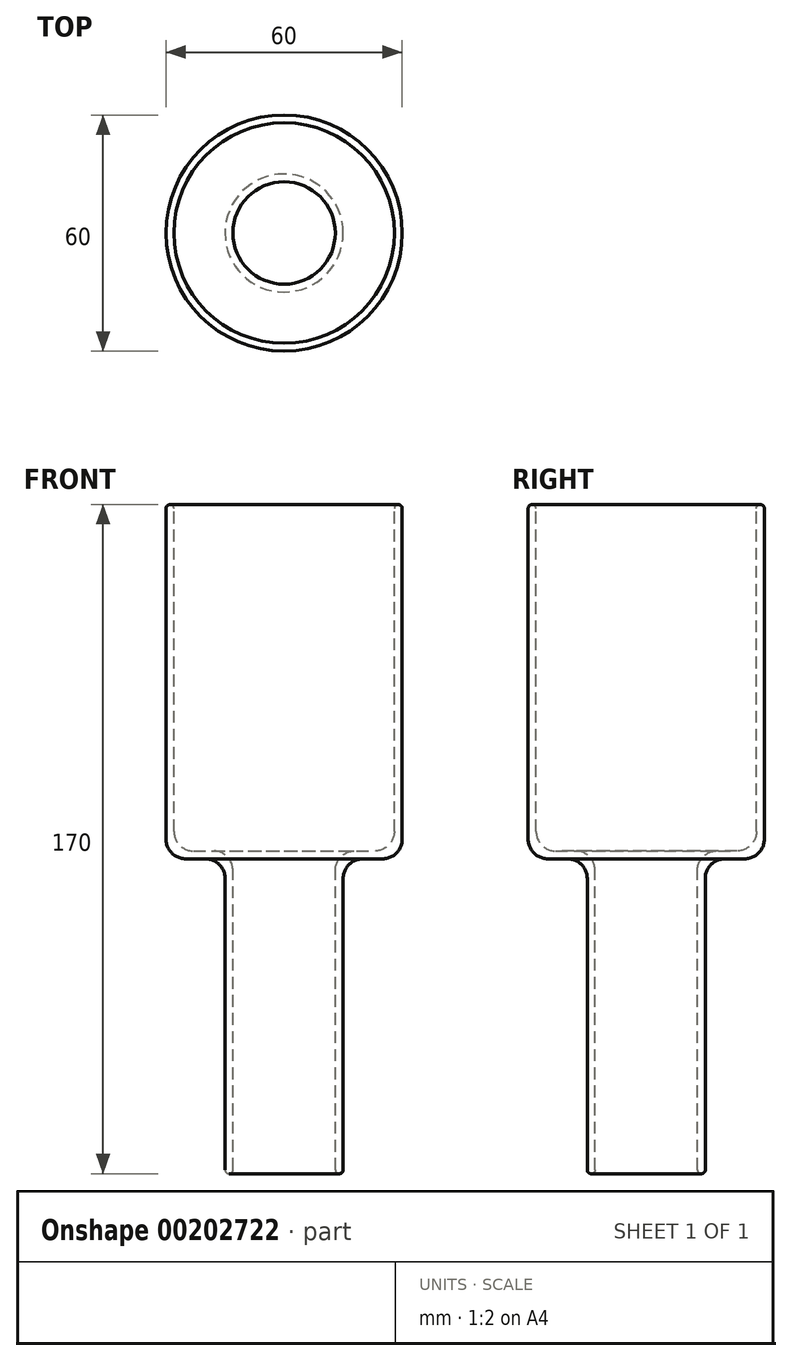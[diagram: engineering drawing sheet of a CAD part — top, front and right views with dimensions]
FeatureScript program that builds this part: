
annotation { "Feature Type Name" : "Feature", "Feature Type Description" : "" }
export const myFeature = defineFeature(function(context is Context, id is Id, definition is map)
    precondition{}
    {
        {
            var Q0;
            Q0=qCreatedBy(makeId("Front.planeOp"),FACE);
            var sketch = newSketch(context, id + "F0", { "sketchPlane" : qUnion([Q0])});
            skLineSegment(sketch, "E0", {"start": v(-28, 98.38) * mm, "end": v(-30, 98.38) * mm});
            skLineSegment(sketch, "E1", {"start": v(-30, 98.38) * mm, "end": v(-30, 8.38) * mm});
            skLineSegment(sketch, "E2", {"start": v(-30, 8.38) * mm, "end": v(-15, 8.38) * mm});
            skLineSegment(sketch, "E3", {"start": v(-15, 8.38) * mm, "end": v(-15, -71.62) * mm});
            skLineSegment(sketch, "E4", {"start": v(-15, -71.62) * mm, "end": v(-13, -71.62) * mm});
            skLineSegment(sketch, "E5.0", {"start": v(-13, 10.38) * mm, "end": v(-13, -71.62) * mm});
            skLineSegment(sketch, "E5.1", {"start": v(-28, 10.38) * mm, "end": v(-13, 10.38) * mm});
            skLineSegment(sketch, "E5.2", {"start": v(-28, 98.38) * mm, "end": v(-28, 10.38) * mm});
            skPoint(sketch, "E6.start.orphan", {"position": v(0, 98.38) * mm});
            skPoint(sketch, "E7.orphan", {"position": v(0, -71.62) * mm});
            skLineSegment(sketch, "E8", {"start": v(0, 98.38) * mm, "end": v(0, -71.62) * mm});
            skSolve(sketch);
        }
        {
            var Q0;
            Q0 = qSketchRegion(id + "F0", true);
            var Q1;
            Q1=sQuery(id+"F0.wireOp",EDGE,"E8");
            revolve(context, id + "F1", {"entities" : qUnion([Q0]), "axis" : qUnion([Q1]), "revolveType" : RevolveType.FULL});
        }
        {
            var Q0;
            Q0=makeQuery(id+"F1.opRevolve","SWEPT_EDGE",EDGE,{"disambiguationData":[OSD([sQuery(id+"F0.wireOp",EDGE,"E1"),sQuery(id+"F0.wireOp",EDGE,"E2")])]});
            var Q1;
            Q1=makeQuery(id+"F1.opRevolve","SWEPT_EDGE",EDGE,{"disambiguationData":[OSD([sQuery(id+"F0.wireOp",EDGE,"E2"),sQuery(id+"F0.wireOp",EDGE,"E3")])]});
            var Q2;
            Q2=makeQuery(id+"F1.opRevolve","SWEPT_EDGE",EDGE,{"disambiguationData":[OSD([sQuery(id+"F0.wireOp",EDGE,"E5.1"),sQuery(id+"F0.wireOp",EDGE,"E5.2")])]});
            var Q3;
            Q3=makeQuery(id+"F1.opRevolve","SWEPT_EDGE",EDGE,{"disambiguationData":[OSD([sQuery(id+"F0.wireOp",EDGE,"E5.0"),sQuery(id+"F0.wireOp",EDGE,"E5.1")])]});
            fillet(context, id + "F2", {"entities" : qUnion([Q0, Q1, Q2, Q3]), "radius" : 5 * mm, "tangentPropagation" : true, "allowEdgeOverflow" : false});
        }
        {
            var Q0;
            Q0=makeQuery(id+"F1.opRevolve","SWEPT_FACE",FACE,{"disambiguationData":[OSD([sQuery(id+"F0.wireOp",EDGE,"E0")])]});
            var Q1;
            Q1=makeQuery(id+"F1.opRevolve","SWEPT_FACE",FACE,{"disambiguationData":[OSD([sQuery(id+"F0.wireOp",EDGE,"E4")])]});
            fillet(context, id + "F3", {"entities" : qUnion([Q0, Q1]), "radius" : 1 * mm, "tangentPropagation" : true, "allowEdgeOverflow" : false});
        }
    });
